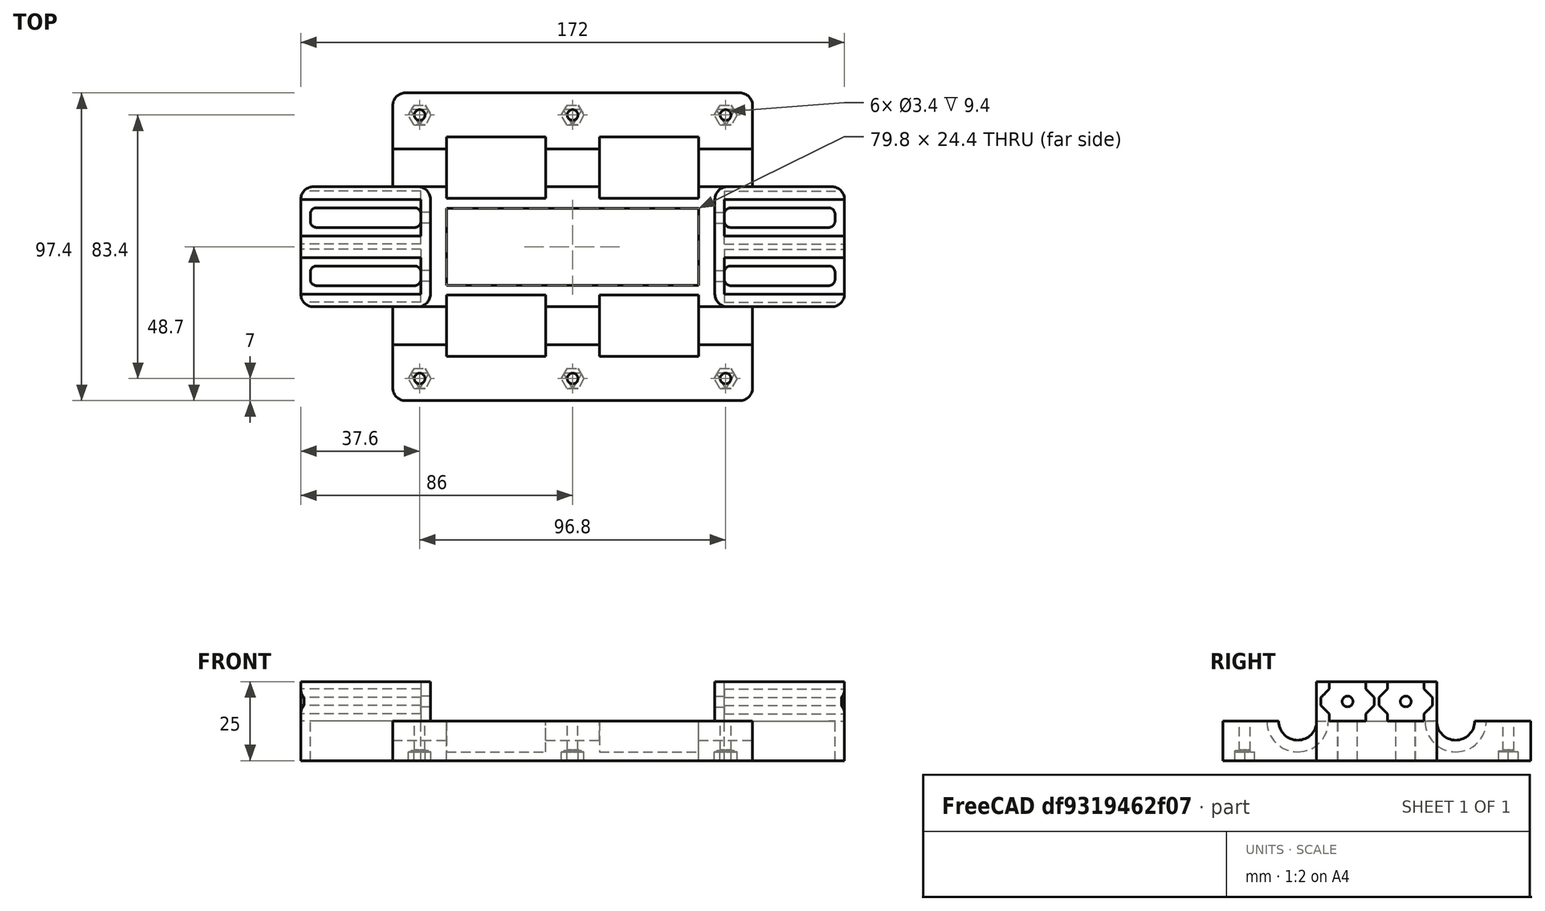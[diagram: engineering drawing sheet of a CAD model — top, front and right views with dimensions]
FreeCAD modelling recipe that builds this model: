
FCSTD DOCUMENT  (FreeCAD 0.17R13541 (Git))
Label: Carrito Parte Inferior
License: All rights reserved
LicenseURL: http://en.wikipedia.org/wiki/All_rights_reserved
objects: Part::Prism×36, Part::Cylinder×26, Part::MultiFuse×15, Part::Common×12, Part::Box×5, Part::Fillet×4, Part::Polygon×2, Part::Extrusion×2, Part::Cut×2, Part::FeaturePython×2, Part::Fuse×1
note: 107 computed .brp shape members not serialized (recipe doc carries the construction recipe); baked Part::Feature solids carry a one-line shape summary decoded from their .brp

FEATURE [Part::Polygon] gt2clamp0_baseof_plane_yz
  Close = true
  Nodes = (12) [(0,2.20417,0),(0,2.20417,2.34375),(0,-0.4,4.94792),(0,-0.4,7.55208),(0,2.20417,10.1562),(0,2.20417,12.5),(0,13.8042,12.5),(0,13.8042,10.1562),+4 more]
FEATURE [Part::Polygon] gt2clamp1_baseof_plane_yz
  Close = true
  Nodes = (12) [(0,2.20417,0),(0,2.20417,2.34375),(0,-0.4,4.94792),(0,-0.4,7.55208),(0,2.20417,10.1562),(0,2.20417,12.5),(0,13.8042,12.5),(0,13.8042,10.1562),+4 more]
FEATURE [Part::Box] inrect
  AttacherType = Attacher::AttachEngine3D
  Height = 14.5
  Length = 79.8
  Placement = pos=(-39.9,-12.2,-1) rot=(0,0,1;0rad)
  Width = 24.4
FEATURE [Part::Box] carlow_box
  AttacherType = Attacher::AttachEngine3D
  Height = 12.5
  Length = 113.8
  Placement = pos=(-56.9,-48.7,0) rot=(0,0,1;0rad)
  Width = 97.4
FEATURE [Part::Cylinder] rod_n
  Angle = 360
  AttacherType = Attacher::AttachEngine3D
  Height = 115.8
  Placement = pos=(-57.9,-25,12.5) rot=(0,1,0;1.5708rad)
  Radius = 6
FEATURE [Part::Cylinder] bearing_1
  Angle = 360
  AttacherType = Attacher::AttachEngine3D
  Height = 31.4
  Placement = pos=(-39.9,25,12.5) rot=(0,1,0;1.5708rad)
  Radius = 9.7
FEATURE [Part::Cylinder] rod_p
  Angle = 360
  AttacherType = Attacher::AttachEngine3D
  Height = 115.8
  Placement = pos=(-57.9,25,12.5) rot=(0,1,0;1.5708rad)
  Radius = 6
FEATURE [Part::Cylinder] bearing_0
  Angle = 360
  AttacherType = Attacher::AttachEngine3D
  Height = 31.4
  Placement = pos=(8.5,25,12.5) rot=(0,1,0;1.5708rad)
  Radius = 9.7
FEATURE [Part::Fillet] carlow_box_fllt
  Base = -> carlow_box
  Edges = 4 edges r=4: [Edge1,Edge3,Edge5,Edge7]
FEATURE [Part::Cylinder] bearing_2
  Angle = 360
  AttacherType = Attacher::AttachEngine3D
  Height = 31.4
  Placement = pos=(8.5,-25,12.5) rot=(0,1,0;1.5708rad)
  Radius = 9.7
FEATURE [Part::Cylinder] bearing_3
  Angle = 360
  AttacherType = Attacher::AttachEngine3D
  Height = 31.4
  Placement = pos=(-39.9,-25,12.5) rot=(0,1,0;1.5708rad)
  Radius = 9.7
FEATURE [Part::Extrusion] gt2clamp0_baseof
  Base = -> gt2clamp0_baseof_plane_yz
  Dir = (39,0,0)
  DirMode = 0
  FaceMakerClass = Part::FaceMakerExtrusion
  LengthFwd = 0
  LengthRev = 0
  Placement = pos=(48,1.2,12.5) rot=(0,0,1;0rad)
  Solid = true
  Symmetric = false
FEATURE [Part::Cylinder] m3_bolt_hole_bolt_head004
  Angle = 360
  AttacherType = Attacher::AttachEngine3D
  Height = 4
  Placement = pos=(0,0,22) rot=(0,0,1;0rad)
  Radius = 2.95
FEATURE [Part::Cylinder] m3_bolt_hole_bolt_head002
  Angle = 360
  AttacherType = Attacher::AttachEngine3D
  Height = 4
  Placement = pos=(0,0,22) rot=(0,0,1;0rad)
  Radius = 2.95
FEATURE [Part::Cylinder] m3_bolt_hole_bolt_sup1away002
  Angle = 360
  AttacherType = Attacher::AttachEngine3D
  Height = 3.3
  Placement = pos=(0,0,21.7) rot=(0,0,1;0rad)
  Radius = 2.95
FEATURE [Part::Cylinder] m3_bolt_hole_bolt_sup1away004
  Angle = 360
  AttacherType = Attacher::AttachEngine3D
  Height = 3.3
  Placement = pos=(0,0,21.7) rot=(0,0,1;0rad)
  Radius = 2.95
FEATURE [Part::Cylinder] m3_bolt_hole_bolt_shank002
  Angle = 360
  AttacherType = Attacher::AttachEngine3D
  Height = 27
  Placement = pos=(0,0,-1) rot=(0,0,1;0rad)
  Radius = 1.7
FEATURE [Part::Cylinder] m3_bolt_hole_bolt_sup1away003
  Angle = 360
  AttacherType = Attacher::AttachEngine3D
  Height = 3.3
  Placement = pos=(0,0,21.7) rot=(0,0,1;0rad)
  Radius = 2.95
FEATURE [Part::Cylinder] m3_bolt_hole_bolt_head003
  Angle = 360
  AttacherType = Attacher::AttachEngine3D
  Height = 4
  Placement = pos=(0,0,22) rot=(0,0,1;0rad)
  Radius = 2.95
FEATURE [Part::Cylinder] m3_bolt_hole_bolt_shank004
  Angle = 360
  AttacherType = Attacher::AttachEngine3D
  Height = 27
  Placement = pos=(0,0,-1) rot=(0,0,1;0rad)
  Radius = 1.7
FEATURE [Part::Cylinder] m3_bolt_hole_bolt_shank003
  Angle = 360
  AttacherType = Attacher::AttachEngine3D
  Height = 27
  Placement = pos=(0,0,-1) rot=(0,0,1;0rad)
  Radius = 1.7
FEATURE [Part::Prism] m3_bolt_hole_bolt_sup2002
  AttacherType = Attacher::AttachEngine3D
  Circumradius = 1.955
  Height = 3.6
  Placement = pos=(0,0,21.4) rot=(0,0,1;0rad)
  Polygon = 6
FEATURE [Part::Prism] m3_bolt_hole_nut002
  AttacherType = Attacher::AttachEngine3D
  Circumradius = 3.605
  Height = 3.8
  Placement = pos=(0,0,-1) rot=(0,0,1;0rad)
  Polygon = 6
FEATURE [Part::Prism] m3_bolt_hole_supnut1away
  AttacherType = Attacher::AttachEngine3D
  Circumradius = 3.605
  Height = 3.1
  Polygon = 6
FEATURE [Part::Prism] m3_bolt_hole_nutsup1
  AttacherType = Attacher::AttachEngine3D
  Circumradius = 3.4
  Height = 3.1
  Placement = pos=(0,0,0) rot=(0,0,1;0.523599rad)
  Polygon = 3
FEATURE [Part::Common] supnut1_cut001
  Base = -> m3_bolt_hole_nutsup1
  Tool = -> m3_bolt_hole_supnut1away
FEATURE [Part::Prism] m3_bolt_hole_bolt_sup1002
  AttacherType = Attacher::AttachEngine3D
  Circumradius = 3.4
  Height = 3.3
  Placement = pos=(0,0,21.7) rot=(0,0,1;0.523599rad)
  Polygon = 3
FEATURE [Part::Common] sup1cut003
  Base = -> m3_bolt_hole_bolt_sup1002
  Tool = -> m3_bolt_hole_bolt_sup1away002
FEATURE [Part::MultiFuse] m3_bolt_hole_bolt002
  Shapes = -> [m3_bolt_hole_bolt_shank002,m3_bolt_hole_bolt_head002,sup1cut003,m3_bolt_hole_bolt_sup2002]
FEATURE [Part::Prism] m3_bolt_hole_bolt_sup1003
  AttacherType = Attacher::AttachEngine3D
  Circumradius = 3.4
  Height = 3.3
  Placement = pos=(0,0,21.7) rot=(0,0,1;0.523599rad)
  Polygon = 3
FEATURE [Part::Common] sup1cut004
  Base = -> m3_bolt_hole_bolt_sup1003
  Tool = -> m3_bolt_hole_bolt_sup1away003
FEATURE [Part::Prism] m3_bolt_hole_bolt_sup2003
  AttacherType = Attacher::AttachEngine3D
  Circumradius = 1.955
  Height = 3.6
  Placement = pos=(0,0,21.4) rot=(0,0,1;0rad)
  Polygon = 6
FEATURE [Part::MultiFuse] m3_bolt_hole_bolt003
  Shapes = -> [m3_bolt_hole_bolt_shank003,m3_bolt_hole_bolt_head003,sup1cut004,m3_bolt_hole_bolt_sup2003]
FEATURE [Part::Prism] m3_bolt_hole_nut003
  AttacherType = Attacher::AttachEngine3D
  Circumradius = 3.605
  Height = 3.8
  Placement = pos=(0,0,-1) rot=(0,0,1;0rad)
  Polygon = 6
FEATURE [Part::Prism] m3_bolt_hole_supnut2
  AttacherType = Attacher::AttachEngine3D
  Circumradius = 1.955
  Height = 3.4
  Polygon = 6
FEATURE [Part::MultiFuse] boltnut003
  Placement = pos=(48.4,41.7,0) rot=(0,0,1;0rad)
  Shapes = -> [m3_bolt_hole_bolt002,m3_bolt_hole_nut002,supnut1_cut001,m3_bolt_hole_supnut2]
FEATURE [Part::Prism] m3_bolt_hole_supnut2001
  AttacherType = Attacher::AttachEngine3D
  Circumradius = 1.955
  Height = 3.4
  Polygon = 6
FEATURE [Part::Prism] m3_bolt_hole_supnut1away001
  AttacherType = Attacher::AttachEngine3D
  Circumradius = 3.605
  Height = 3.1
  Polygon = 6
FEATURE [Part::Prism] m3_bolt_hole_nutsup1001
  AttacherType = Attacher::AttachEngine3D
  Circumradius = 3.4
  Height = 3.1
  Placement = pos=(0,0,0) rot=(0,0,1;0.523599rad)
  Polygon = 3
FEATURE [Part::Common] supnut1_cut002
  Base = -> m3_bolt_hole_nutsup1001
  Tool = -> m3_bolt_hole_supnut1away001
FEATURE [Part::MultiFuse] boltnut004
  Placement = pos=(0,41.7,0) rot=(0,0,1;0rad)
  Shapes = -> [m3_bolt_hole_bolt003,m3_bolt_hole_nut003,supnut1_cut002,m3_bolt_hole_supnut2001]
FEATURE [Part::Prism] m3_bolt_hole_bolt_sup1004
  AttacherType = Attacher::AttachEngine3D
  Circumradius = 3.4
  Height = 3.3
  Placement = pos=(0,0,21.7) rot=(0,0,1;0.523599rad)
  Polygon = 3
FEATURE [Part::Common] sup1cut005
  Base = -> m3_bolt_hole_bolt_sup1004
  Tool = -> m3_bolt_hole_bolt_sup1away004
FEATURE [Part::Prism] m3_bolt_hole_bolt_sup2004
  AttacherType = Attacher::AttachEngine3D
  Circumradius = 1.955
  Height = 3.6
  Placement = pos=(0,0,21.4) rot=(0,0,1;0rad)
  Polygon = 6
FEATURE [Part::MultiFuse] m3_bolt_hole_bolt004
  Shapes = -> [m3_bolt_hole_bolt_shank004,m3_bolt_hole_bolt_head004,sup1cut005,m3_bolt_hole_bolt_sup2004]
FEATURE [Part::Prism] m3_bolt_hole_supnut1away002
  AttacherType = Attacher::AttachEngine3D
  Circumradius = 3.605
  Height = 3.1
  Polygon = 6
FEATURE [Part::Prism] m3_bolt_hole_supnut2002
  AttacherType = Attacher::AttachEngine3D
  Circumradius = 1.955
  Height = 3.4
  Polygon = 6
FEATURE [Part::Prism] m3_bolt_hole_nut004
  AttacherType = Attacher::AttachEngine3D
  Circumradius = 3.605
  Height = 3.8
  Placement = pos=(0,0,-1) rot=(0,0,1;0rad)
  Polygon = 6
FEATURE [Part::Prism] m3_bolt_hole_bolt_sup1005
  AttacherType = Attacher::AttachEngine3D
  Circumradius = 3.4
  Height = 3.3
  Placement = pos=(0,0,21.7) rot=(0,0,1;0.523599rad)
  Polygon = 3
FEATURE [Part::Prism] m3_bolt_hole_nutsup1002
  AttacherType = Attacher::AttachEngine3D
  Circumradius = 3.4
  Height = 3.1
  Placement = pos=(0,0,0) rot=(0,0,1;0.523599rad)
  Polygon = 3
FEATURE [Part::Common] supnut1_cut003
  Base = -> m3_bolt_hole_nutsup1002
  Tool = -> m3_bolt_hole_supnut1away002
FEATURE [Part::MultiFuse] boltnut005
  Placement = pos=(-48.4,41.7,0) rot=(0,0,1;0rad)
  Shapes = -> [m3_bolt_hole_bolt004,m3_bolt_hole_nut004,supnut1_cut003,m3_bolt_hole_supnut2002]
FEATURE [Part::Cylinder] m3_bolt_hole_bolt_head005
  Angle = 360
  AttacherType = Attacher::AttachEngine3D
  Height = 4
  Placement = pos=(0,0,22) rot=(0,0,1;0rad)
  Radius = 2.95
FEATURE [Part::Cylinder] m3_bolt_hole_bolt_sup1away006
  Angle = 360
  AttacherType = Attacher::AttachEngine3D
  Height = 3.3
  Placement = pos=(0,0,21.7) rot=(0,0,1;0rad)
  Radius = 2.95
FEATURE [Part::Cylinder] m3_bolt_hole_bolt_head007
  Angle = 360
  AttacherType = Attacher::AttachEngine3D
  Height = 4
  Placement = pos=(0,0,22) rot=(0,0,1;0rad)
  Radius = 2.95
FEATURE [Part::Cylinder] m3_bolt_hole_bolt_sup1away007
  Angle = 360
  AttacherType = Attacher::AttachEngine3D
  Height = 3.3
  Placement = pos=(0,0,21.7) rot=(0,0,1;0rad)
  Radius = 2.95
FEATURE [Part::Cylinder] m3_bolt_hole_bolt_shank005
  Angle = 360
  AttacherType = Attacher::AttachEngine3D
  Height = 27
  Placement = pos=(0,0,-1) rot=(0,0,1;0rad)
  Radius = 1.7
FEATURE [Part::Cylinder] m3_bolt_hole_bolt_sup1away005
  Angle = 360
  AttacherType = Attacher::AttachEngine3D
  Height = 3.3
  Placement = pos=(0,0,21.7) rot=(0,0,1;0rad)
  Radius = 2.95
FEATURE [Part::Common] sup1cut006
  Base = -> m3_bolt_hole_bolt_sup1005
  Tool = -> m3_bolt_hole_bolt_sup1away005
FEATURE [Part::Cylinder] m3_bolt_hole_bolt_shank006
  Angle = 360
  AttacherType = Attacher::AttachEngine3D
  Height = 27
  Placement = pos=(0,0,-1) rot=(0,0,1;0rad)
  Radius = 1.7
FEATURE [Part::Cylinder] m3_bolt_hole_bolt_head006
  Angle = 360
  AttacherType = Attacher::AttachEngine3D
  Height = 4
  Placement = pos=(0,0,22) rot=(0,0,1;0rad)
  Radius = 2.95
FEATURE [Part::Cylinder] m3_bolt_hole_bolt_shank007
  Angle = 360
  AttacherType = Attacher::AttachEngine3D
  Height = 27
  Placement = pos=(0,0,-1) rot=(0,0,1;0rad)
  Radius = 1.7
FEATURE [Part::Prism] m3_bolt_hole_nut005
  AttacherType = Attacher::AttachEngine3D
  Circumradius = 3.605
  Height = 3.8
  Placement = pos=(0,0,-1) rot=(0,0,1;0rad)
  Polygon = 6
FEATURE [Part::Prism] m3_bolt_hole_supnut1away003
  AttacherType = Attacher::AttachEngine3D
  Circumradius = 3.605
  Height = 3.1
  Polygon = 6
FEATURE [Part::Prism] m3_bolt_hole_supnut2003
  AttacherType = Attacher::AttachEngine3D
  Circumradius = 1.955
  Height = 3.4
  Polygon = 6
FEATURE [Part::Prism] m3_bolt_hole_nutsup1003
  AttacherType = Attacher::AttachEngine3D
  Circumradius = 3.4
  Height = 3.1
  Placement = pos=(0,0,0) rot=(0,0,1;0.523599rad)
  Polygon = 3
FEATURE [Part::Common] supnut1_cut004
  Base = -> m3_bolt_hole_nutsup1003
  Tool = -> m3_bolt_hole_supnut1away003
FEATURE [Part::Prism] m3_bolt_hole_bolt_sup2005
  AttacherType = Attacher::AttachEngine3D
  Circumradius = 1.955
  Height = 3.6
  Placement = pos=(0,0,21.4) rot=(0,0,1;0rad)
  Polygon = 6
FEATURE [Part::MultiFuse] m3_bolt_hole_bolt005
  Shapes = -> [m3_bolt_hole_bolt_shank005,m3_bolt_hole_bolt_head005,sup1cut006,m3_bolt_hole_bolt_sup2005]
FEATURE [Part::MultiFuse] boltnut006
  Placement = pos=(48.4,-41.7,0) rot=(0,0,1;0rad)
  Shapes = -> [m3_bolt_hole_bolt005,m3_bolt_hole_nut005,supnut1_cut004,m3_bolt_hole_supnut2003]
FEATURE [Part::Prism] m3_bolt_hole_nutsup1004
  AttacherType = Attacher::AttachEngine3D
  Circumradius = 3.4
  Height = 3.1
  Placement = pos=(0,0,0) rot=(0,0,1;0.523599rad)
  Polygon = 3
FEATURE [Part::Prism] m3_bolt_hole_bolt_sup1006
  AttacherType = Attacher::AttachEngine3D
  Circumradius = 3.4
  Height = 3.3
  Placement = pos=(0,0,21.7) rot=(0,0,1;0.523599rad)
  Polygon = 3
FEATURE [Part::Common] sup1cut007
  Base = -> m3_bolt_hole_bolt_sup1006
  Tool = -> m3_bolt_hole_bolt_sup1away006
FEATURE [Part::Prism] m3_bolt_hole_bolt_sup2006
  AttacherType = Attacher::AttachEngine3D
  Circumradius = 1.955
  Height = 3.6
  Placement = pos=(0,0,21.4) rot=(0,0,1;0rad)
  Polygon = 6
FEATURE [Part::MultiFuse] m3_bolt_hole_bolt006
  Shapes = -> [m3_bolt_hole_bolt_shank006,m3_bolt_hole_bolt_head006,sup1cut007,m3_bolt_hole_bolt_sup2006]
FEATURE [Part::Prism] m3_bolt_hole_nut006
  AttacherType = Attacher::AttachEngine3D
  Circumradius = 3.605
  Height = 3.8
  Placement = pos=(0,0,-1) rot=(0,0,1;0rad)
  Polygon = 6
FEATURE [Part::Prism] m3_bolt_hole_supnut1away004
  AttacherType = Attacher::AttachEngine3D
  Circumradius = 3.605
  Height = 3.1
  Polygon = 6
FEATURE [Part::Common] supnut1_cut005
  Base = -> m3_bolt_hole_nutsup1004
  Tool = -> m3_bolt_hole_supnut1away004
FEATURE [Part::Prism] m3_bolt_hole_bolt_sup2007
  AttacherType = Attacher::AttachEngine3D
  Circumradius = 1.955
  Height = 3.6
  Placement = pos=(0,0,21.4) rot=(0,0,1;0rad)
  Polygon = 6
FEATURE [Part::Prism] m3_bolt_hole_nut007
  AttacherType = Attacher::AttachEngine3D
  Circumradius = 3.605
  Height = 3.8
  Placement = pos=(0,0,-1) rot=(0,0,1;0rad)
  Polygon = 6
FEATURE [Part::Prism] m3_bolt_hole_supnut2004
  AttacherType = Attacher::AttachEngine3D
  Circumradius = 1.955
  Height = 3.4
  Polygon = 6
FEATURE [Part::MultiFuse] boltnut007
  Placement = pos=(0,-41.7,0) rot=(0,0,1;0rad)
  Shapes = -> [m3_bolt_hole_bolt006,m3_bolt_hole_nut006,supnut1_cut005,m3_bolt_hole_supnut2004]
FEATURE [Part::Prism] m3_bolt_hole_bolt_sup1007
  AttacherType = Attacher::AttachEngine3D
  Circumradius = 3.4
  Height = 3.3
  Placement = pos=(0,0,21.7) rot=(0,0,1;0.523599rad)
  Polygon = 3
FEATURE [Part::Common] sup1cut008
  Base = -> m3_bolt_hole_bolt_sup1007
  Tool = -> m3_bolt_hole_bolt_sup1away007
FEATURE [Part::MultiFuse] m3_bolt_hole_bolt007
  Shapes = -> [m3_bolt_hole_bolt_shank007,m3_bolt_hole_bolt_head007,sup1cut008,m3_bolt_hole_bolt_sup2007]
FEATURE [Part::Prism] m3_bolt_hole_nutsup1005
  AttacherType = Attacher::AttachEngine3D
  Circumradius = 3.4
  Height = 3.1
  Placement = pos=(0,0,0) rot=(0,0,1;0.523599rad)
  Polygon = 3
FEATURE [Part::Prism] m3_bolt_hole_supnut2005
  AttacherType = Attacher::AttachEngine3D
  Circumradius = 1.955
  Height = 3.4
  Polygon = 6
FEATURE [Part::Prism] m3_bolt_hole_supnut1away005
  AttacherType = Attacher::AttachEngine3D
  Circumradius = 3.605
  Height = 3.1
  Polygon = 6
FEATURE [Part::Common] supnut1_cut006
  Base = -> m3_bolt_hole_nutsup1005
  Tool = -> m3_bolt_hole_supnut1away005
FEATURE [Part::MultiFuse] boltnut008
  Placement = pos=(-48.4,-41.7,0) rot=(0,0,1;0rad)
  Shapes = -> [m3_bolt_hole_bolt007,m3_bolt_hole_nut007,supnut1_cut006,m3_bolt_hole_supnut2005]
FEATURE [Part::Box] bccr_box
  AttacherType = Attacher::AttachEngine3D
  Height = 25
  Length = 41
  Placement = pos=(45,-19,0) rot=(0,0,1;0rad)
  Width = 38
FEATURE [Part::Fillet] bccr_fllt
  Base = -> bccr_box
  Edges = 4 edges r=4: [Edge1,Edge3,Edge5,Edge7]
FEATURE [Part::Extrusion] gt2clamp1_baseof
  Base = -> gt2clamp1_baseof_plane_yz
  Dir = (39,0,0)
  DirMode = 0
  FaceMakerClass = Part::FaceMakerExtrusion
  LengthFwd = 0
  LengthRev = 0
  Placement = pos=(48,-17.2083,12.5) rot=(0,0,1;0rad)
  Solid = true
  Symmetric = false
FEATURE [Part::Box] bccr_bthole1
  AttacherType = Attacher::AttachEngine3D
  Height = 14.5
  Length = 35
  Placement = pos=(0,-3.12193,0) rot=(0,0,1;0rad)
  Width = 6.24386
FEATURE [Part::Fillet] bccr_bthole1_fllt
  Base = -> bccr_bthole1
  Edges = 4 edges r=2: [Edge1,Edge3,Edge5,Edge7]
  Placement = pos=(48,-9.20417,-1) rot=(0,0,1;0rad)
FEATURE [Part::Cylinder] bccr_bolthole0
  Angle = 360
  AttacherType = Attacher::AttachEngine3D
  Height = 5
  Placement = pos=(44,9.20417,18.75) rot=(0,1,0;1.5708rad)
  Radius = 1.7
FEATURE [Part::Cylinder] bccr_bolthole1
  Angle = 360
  AttacherType = Attacher::AttachEngine3D
  Height = 5
  Placement = pos=(44,-9.20417,18.75) rot=(0,1,0;1.5708rad)
  Radius = 1.7
FEATURE [Part::Box] bccr_bthole0
  AttacherType = Attacher::AttachEngine3D
  Height = 14.5
  Length = 35
  Placement = pos=(0,-3.12193,0) rot=(0,0,1;0rad)
  Width = 6.24386
FEATURE [Part::Fillet] bccr_bthole0_fllt
  Base = -> bccr_bthole0
  Edges = 4 edges r=2: [Edge1,Edge3,Edge5,Edge7]
  Placement = pos=(48,9.20417,-1) rot=(0,0,1;0rad)
FEATURE [Part::MultiFuse] bccr_holes
  Shapes = -> [gt2clamp0_baseof,gt2clamp1_baseof,bccr_bthole0_fllt,bccr_bthole1_fllt,bccr_bolthole0,bccr_bolthole1]
FEATURE [Part::Cut] bccr_final
  Base = -> bccr_fllt
  Tool = -> bccr_holes
FEATURE [Part::Fuse] bccr_bthole_fused
  Base = -> bccr_bthole0_fllt
  Tool = -> bccr_bthole1_fllt
FEATURE [Part::FeaturePython] Clone003  label="Clone of bccr_final"  # Draft clone (typed FeaturePython)
  Objects = -> [bccr_final]
  Placement = pos=(0,0,0) rot=(0,0,1;3.14159rad)
  Scale = (1,1,1)
FEATURE [Part::FeaturePython] Clone002  label="Clone of bccr_bthole_fused"  # Draft clone (typed FeaturePython)
  Objects = -> [bccr_bthole_fused]
  Placement = pos=(0,0,0) rot=(0,0,1;3.14159rad)
  Scale = (1,1,1)
FEATURE [Part::MultiFuse] fuse_lowcar_holes
  Shapes = -> [inrect,rod_n,rod_p,bearing_0,bearing_1,bearing_2,bearing_3,boltnut003,boltnut004,boltnut005,boltnut006,boltnut007,boltnut008,bccr_bthole_fused,Clone002]
FEATURE [Part::Cut] lowcar_hole
  Base = -> carlow_box_fllt
  Tool = -> fuse_lowcar_holes
FEATURE [Part::MultiFuse] lowcar_bccr
  Shapes = -> [lowcar_hole,bccr_final,Clone003]
